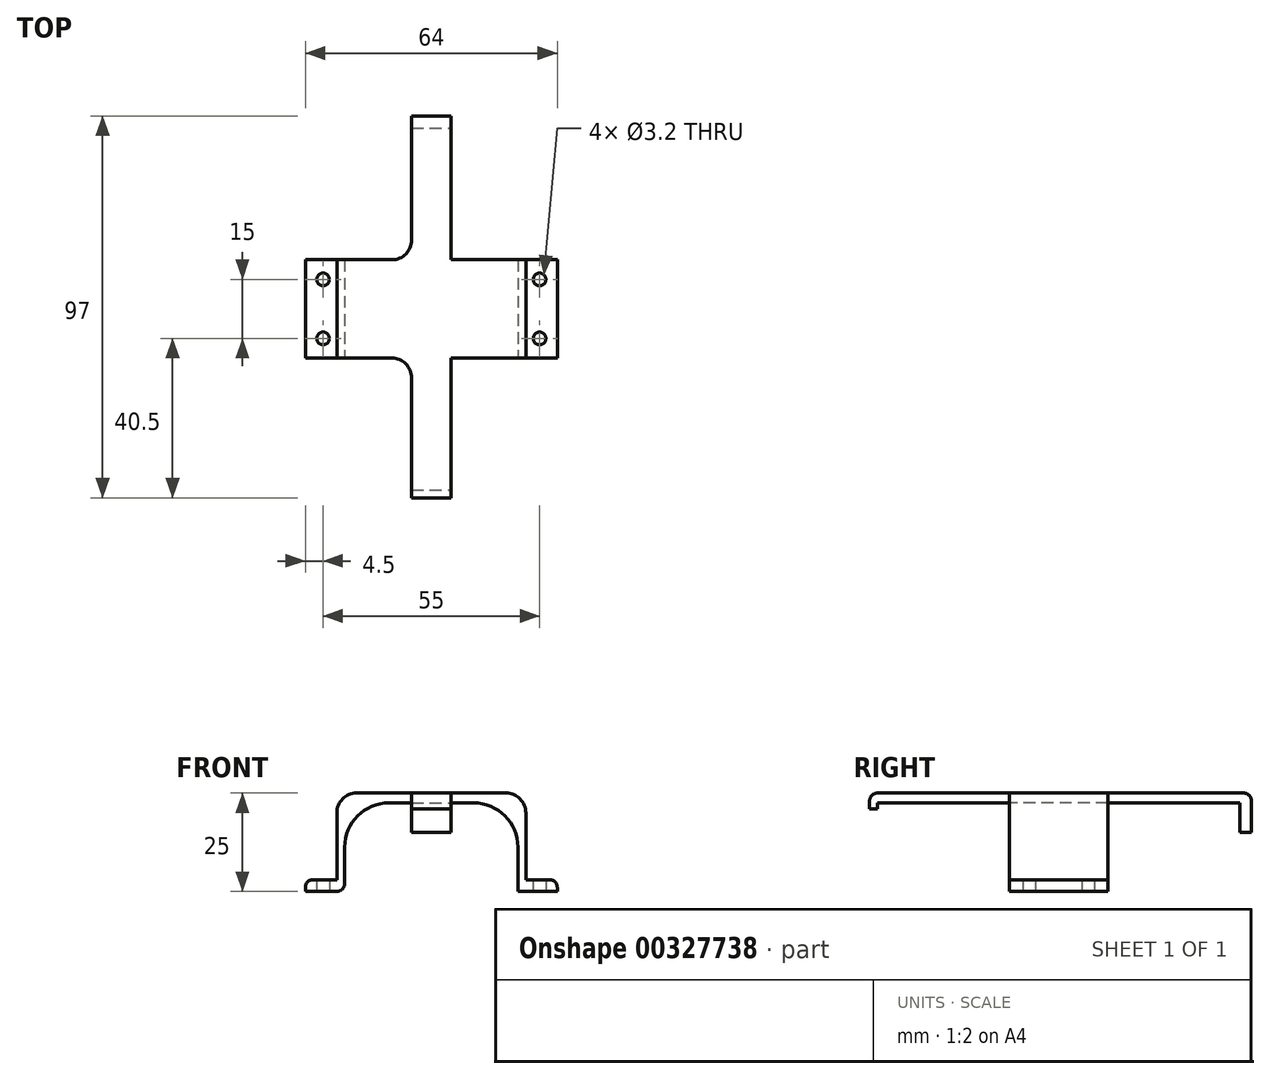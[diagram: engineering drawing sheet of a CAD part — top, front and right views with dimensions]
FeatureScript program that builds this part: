
annotation { "Feature Type Name" : "Feature", "Feature Type Description" : "" }
export const myFeature = defineFeature(function(context is Context, id is Id, definition is map)
    precondition{}
    {
        {
            var Q0;
            Q0=qCreatedBy(makeId("Front.planeOp"),FACE);
            var sketch = newSketch(context, id + "F0", { "sketchPlane" : qUnion([Q0])});
            skLineSegment(sketch, "E0.bottom", {"start": v(-24, 12.5) * mm, "end": v(24, 12.5) * mm});
            skLineSegment(sketch, "E0.top", {"start": v(-24, -12.5) * mm, "end": v(24, -12.5) * mm});
            skLineSegment(sketch, "E0.left", {"start": v(-24, 12.5) * mm, "end": v(-24, -12.5) * mm});
            skLineSegment(sketch, "E0.right", {"start": v(24, 12.5) * mm, "end": v(24, -12.5) * mm});
            skPoint(sketch, "E1", {"position": v(0, 12.5) * mm});
            skPoint(sketch, "E2", {"position": v(-24, 0) * mm});
            skSolve(sketch);
        }
        {
            var Q0;
            Q0=makeQuery(id+"F0.imprint","IMPRINT",FACE,{"disambiguationData":[TD([[makeQuery(id+"F0.imprint","IMPRINT",EDGE,{"derivedFrom":sQuery(id+"F0.wireOp",EDGE,"E0.bottom")}),-1.0]])]});
            extrude(context, id + "F1", {"entities" : qUnion([Q0]), "oppositeDirection" : true, "depth" : 25 * mm});
        }
        {
            var Q0;
            Q0=makeQuery(id+"F1.opExtrude","CAP_FACE",FACE,{"disambiguationData":[OSD([sQuery(id+"F0.wireOp",EDGE,"E0.bottom"),sQuery(id+"F0.wireOp",EDGE,"E0.top"),sQuery(id+"F0.wireOp",EDGE,"E0.left"),sQuery(id+"F0.wireOp",EDGE,"E0.right")])],"isStart":true});
            var sketch = newSketch(context, id + "F2", { "sketchPlane" : qUnion([Q0])});
            skArc(sketch, "E3", {"start": v(-10.75, -12.5) * mm, "mid": v(-22, -1.25) * mm, "end": v(-10.75, 10) * mm});
            skArc(sketch, "E4", {"start": v(10.75, -12.5) * mm, "mid": v(22, -1.25) * mm, "end": v(10.75, 10) * mm});
            skPoint(sketch, "E5", {"position": v(-22, -1.25) * mm});
            skPoint(sketch, "E6", {"position": v(22, -1.25) * mm});
            skLineSegment(sketch, "E7", {"start": v(-10.75, 10) * mm, "end": v(10.75, 10) * mm});
            skLineSegment(sketch, "E8", {"start": v(10.75, -12.5) * mm, "end": v(-10.75, -12.5) * mm});
            skPoint(sketch, "E9", {"position": v(0, 10) * mm});
            skLineSegment(sketch, "E10", {"start": v(-22, -1.25) * mm, "end": v(-22, -12.5) * mm});
            skLineSegment(sketch, "E11", {"start": v(-22, -12.5) * mm, "end": v(22, -12.5) * mm});
            skLineSegment(sketch, "E12", {"start": v(22, -12.5) * mm, "end": v(22, -1.25) * mm});
            skSolve(sketch);
        }
        {
            var Q0;
            {var subQ0=sQuery(id+"F2.wireOp",EDGE,"E7");Q0=makeQuery(id+"F2.imprint","IMPRINT",FACE,{"disambiguationData":[TD([[makeQuery(id+"F2.imprint","IMPRINT",EDGE,{"derivedFrom":subQ0}),-1.0]])]});}
            var Q1;
            {var subQ3=sQuery(id+"F2.wireOp",EDGE,"E10");Q1=makeQuery(id+"F2.imprint","IMPRINT",FACE,{"disambiguationData":[TD([[makeQuery(id+"F2.imprint","IMPRINT",EDGE,{"derivedFrom":subQ3}),1.0]])]});}
            var Q2;
            {var subQ3=sQuery(id+"F2.wireOp",EDGE,"E12");Q2=makeQuery(id+"F2.imprint","IMPRINT",FACE,{"disambiguationData":[TD([[makeQuery(id+"F2.imprint","IMPRINT",EDGE,{"derivedFrom":subQ3}),1.0]])]});}
            var Q3;
            Q3=makeQuery(id+"F1.opExtrude","CAP_FACE",FACE,{"disambiguationData":[OSD([sQuery(id+"F0.wireOp",EDGE,"E0.bottom"),sQuery(id+"F0.wireOp",EDGE,"E0.top"),sQuery(id+"F0.wireOp",EDGE,"E0.left"),sQuery(id+"F0.wireOp",EDGE,"E0.right")])],"isStart":false});
            extrude(context, id + "F3", {"entities" : qUnion([Q0, Q1, Q2]), "operationType" : NewBodyOperationType.REMOVE, "endBound" : BoundingType.UP_TO_SURFACE, "oppositeDirection" : true, "endBoundEntityFace" : qUnion([Q3]), "depth" : 25 * mm});
        }
        {
            var Q0;
            Q0=makeQuery(id+"F1.opExtrude","SWEPT_FACE",FACE,{"disambiguationData":[OSD([sQuery(id+"F0.wireOp",EDGE,"E0.bottom")])]});
            var sketch = newSketch(context, id + "F4", { "sketchPlane" : qUnion([Q0])});
            skLineSegment(sketch, "E13.bottom", {"start": v(-5, 58.5) * mm, "end": v(5, 58.5) * mm});
            skLineSegment(sketch, "E13.top", {"start": v(-5, -33.5) * mm, "end": v(5, -33.5) * mm});
            skLineSegment(sketch, "E13.left", {"start": v(-5, 58.5) * mm, "end": v(-5, -33.5) * mm});
            skLineSegment(sketch, "E13.right", {"start": v(5, 58.5) * mm, "end": v(5, -33.5) * mm});
            skPoint(sketch, "E14", {"position": v(0, 58.5) * mm});
            skPoint(sketch, "E15", {"position": v(5, 12.5) * mm});
            skPoint(sketch, "E16", {"position": v(24, 12.5) * mm});
            skSolve(sketch);
        }
        {
            var Q0;
            {var subQ0=sQuery(id+"F4.wireOp",EDGE,"E13.bottom");Q0=makeQuery(id+"F4.imprint","IMPRINT",FACE,{"disambiguationData":[TD([[makeQuery(id+"F4.imprint","IMPRINT",EDGE,{"derivedFrom":subQ0}),-1.0]])]});}
            var Q1;
            {var subQ0=sQuery(id+"F4.wireOp",EDGE,"E13.top");Q1=makeQuery(id+"F4.imprint","IMPRINT",FACE,{"disambiguationData":[TD([[makeQuery(id+"F4.imprint","IMPRINT",EDGE,{"derivedFrom":subQ0}),1.0]])]});}
            var Q2;
            Q2=makeQuery(id+"F3.boolean.opBoolean","COPY",FACE,{"derivedFrom":makeQuery(id+"F3.opExtrude","SWEPT_FACE",FACE,{"disambiguationData":[OSD([sQuery(id+"F2.wireOp",EDGE,"E7")])]})});
            extrude(context, id + "F5", {"entities" : qUnion([Q0, Q1]), "operationType" : NewBodyOperationType.ADD, "endBound" : BoundingType.UP_TO_SURFACE, "oppositeDirection" : true, "endBoundEntityFace" : qUnion([Q2]), "depth" : 25 * mm});
        }
        {
            var Q0;
            Q0=makeQuery(id+"F5.opExtrude","SWEPT_FACE",FACE,{"disambiguationData":[OSD([sQuery(id+"F4.wireOp",EDGE,"E13.top")])]});
            var sketch = newSketch(context, id + "F6", { "sketchPlane" : qUnion([Q0])});
            skLineSegment(sketch, "E17.bottom", {"start": v(-5, 12.5) * mm, "end": v(5, 12.5) * mm});
            skLineSegment(sketch, "E17.top", {"start": v(-5, 8.5) * mm, "end": v(5, 8.5) * mm});
            skLineSegment(sketch, "E17.left", {"start": v(-5, 12.5) * mm, "end": v(-5, 8.5) * mm});
            skLineSegment(sketch, "E17.right", {"start": v(5, 12.5) * mm, "end": v(5, 8.5) * mm});
            skSolve(sketch);
        }
        {
            var Q0;
            {var subQ0=sQuery(id+"F6.wireOp",EDGE,"E17.top");Q0=makeQuery(id+"F6.imprint","IMPRINT",FACE,{"disambiguationData":[TD([[makeQuery(id+"F6.imprint","IMPRINT",EDGE,{"derivedFrom":subQ0}),1.0]])]});}
            var Q1;
            {var subQ0=sQuery(id+"F6.wireOp",EDGE,"E17.bottom");Q1=makeQuery(id+"F6.imprint","IMPRINT",FACE,{"disambiguationData":[TD([[makeQuery(id+"F6.imprint","IMPRINT",EDGE,{"derivedFrom":subQ0}),-1.0]])]});}
            extrude(context, id + "F7", {"entities" : qUnion([Q0, Q1]), "operationType" : NewBodyOperationType.ADD, "depth" : 2 * mm});
        }
        {
            var Q0;
            Q0=makeQuery(id+"F5.opExtrude","SWEPT_FACE",FACE,{"disambiguationData":[OSD([sQuery(id+"F4.wireOp",EDGE,"E13.bottom")])]});
            var sketch = newSketch(context, id + "F8", { "sketchPlane" : qUnion([Q0])});
            skLineSegment(sketch, "E18.bottom", {"start": v(-5, 12.5) * mm, "end": v(5, 12.5) * mm});
            skLineSegment(sketch, "E18.top", {"start": v(-5, 2.5) * mm, "end": v(5, 2.5) * mm});
            skLineSegment(sketch, "E18.left", {"start": v(-5, 12.5) * mm, "end": v(-5, 2.5) * mm});
            skLineSegment(sketch, "E18.right", {"start": v(5, 12.5) * mm, "end": v(5, 2.5) * mm});
            skSolve(sketch);
        }
        {
            var Q0;
            {var subQ0=sQuery(id+"F8.wireOp",EDGE,"E18.top");Q0=makeQuery(id+"F8.imprint","IMPRINT",FACE,{"disambiguationData":[TD([[makeQuery(id+"F8.imprint","IMPRINT",EDGE,{"derivedFrom":subQ0}),1.0]])]});}
            var Q1;
            {var subQ0=sQuery(id+"F8.wireOp",EDGE,"E18.bottom");Q1=makeQuery(id+"F8.imprint","IMPRINT",FACE,{"disambiguationData":[TD([[makeQuery(id+"F8.imprint","IMPRINT",EDGE,{"derivedFrom":subQ0}),1.0]])]});}
            extrude(context, id + "F9", {"entities" : qUnion([Q0, Q1]), "operationType" : NewBodyOperationType.ADD, "depth" : 3 * mm});
        }
        {
            var Q0;
            {var subQ0=sQuery(id+"F0.wireOp",EDGE,"E0.right");var subQ2=sQuery(id+"F0.wireOp",EDGE,"E0.top");Q0=makeQuery(id+"F3.boolean.opBoolean","SPLIT",FACE,{"disambiguationData":[TD([makeQuery(id+"F1.opExtrude","SWEPT_FACE",FACE,{"disambiguationData":[OSD([subQ0])]})])],"derivedFrom":makeQuery(id+"F1.opExtrude","SWEPT_FACE",FACE,{"disambiguationData":[OSD([subQ2])]})});}
            var sketch = newSketch(context, id + "F10", { "sketchPlane" : qUnion([Q0])});
            skLineSegment(sketch, "E19.bottom", {"start": v(24, 0) * mm, "end": v(32, 0) * mm});
            skLineSegment(sketch, "E19.top", {"start": v(24, -25) * mm, "end": v(32, -25) * mm});
            skLineSegment(sketch, "E19.left", {"start": v(24, 0) * mm, "end": v(24, -25) * mm});
            skLineSegment(sketch, "E19.right", {"start": v(32, 0) * mm, "end": v(32, -25) * mm});
            skLineSegment(sketch, "E20.0.0", {"start": v(-24, -25) * mm, "end": v(-22, -25) * mm, "construction": true});
            skLineSegment(sketch, "E20.0.1", {"start": v(-22, -25) * mm, "end": v(-22, 0) * mm, "construction": true});
            skLineSegment(sketch, "E20.0.2", {"start": v(-22, 0) * mm, "end": v(-24, 0) * mm, "construction": true});
            skLineSegment(sketch, "E20.0.3", {"start": v(-24, 0) * mm, "end": v(-24, -25) * mm, "construction": true});
            skLineSegment(sketch, "E21.bottom", {"start": v(-24, 0) * mm, "end": v(-32, 0) * mm});
            skLineSegment(sketch, "E21.top", {"start": v(-24, -25) * mm, "end": v(-32, -25) * mm});
            skLineSegment(sketch, "E21.left", {"start": v(-24, 0) * mm, "end": v(-24, -25) * mm});
            skLineSegment(sketch, "E21.right", {"start": v(-32, 0) * mm, "end": v(-32, -25) * mm});
            skSolve(sketch);
        }
        {
            var Q0;
            Q0=makeQuery(id+"F10.imprint","IMPRINT",FACE,{"disambiguationData":[TD([[makeQuery(id+"F10.imprint","IMPRINT",EDGE,{"derivedFrom":sQuery(id+"F10.wireOp",EDGE,"E21.bottom")}),1.0]])]});
            var Q1;
            Q1=makeQuery(id+"F10.imprint","IMPRINT",FACE,{"disambiguationData":[TD([[makeQuery(id+"F10.imprint","IMPRINT",EDGE,{"derivedFrom":sQuery(id+"F10.wireOp",EDGE,"E19.bottom")}),-1.0]])]});
            extrude(context, id + "F11", {"entities" : qUnion([Q0, Q1]), "operationType" : NewBodyOperationType.ADD, "oppositeDirection" : true, "depth" : 3 * mm});
        }
        {
            var Q0;
            {var subQ0=sQuery(id+"F0.wireOp",EDGE,"E0.right");var subQ2=sQuery(id+"F0.wireOp",EDGE,"E0.top");Q0=makeQuery(id+"F11.boolean.opBoolean","MERGE",FACE,{"derivedFrom":[makeQuery(id+"F3.boolean.opBoolean","SPLIT",FACE,{"disambiguationData":[TD([makeQuery(id+"F1.opExtrude","SWEPT_FACE",FACE,{"disambiguationData":[OSD([subQ0])]})])],"derivedFrom":makeQuery(id+"F1.opExtrude","SWEPT_FACE",FACE,{"disambiguationData":[OSD([subQ2])]})}),makeQuery(id+"F11.opExtrude","CAP_FACE",FACE,{"disambiguationData":[OSD([sQuery(id+"F10.wireOp",EDGE,"E19.bottom"),sQuery(id+"F10.wireOp",EDGE,"E19.top"),sQuery(id+"F10.wireOp",EDGE,"E19.left"),sQuery(id+"F10.wireOp",EDGE,"E19.right")])],"isStart":true})]});}
            var sketch = newSketch(context, id + "F12", { "sketchPlane" : qUnion([Q0])});
            skCircle(sketch, "E22", {"center": v(27.5, -5) * mm, "radius": 1.6 * mm});
            skCircle(sketch, "E23", {"center": v(27.5, -20) * mm, "radius": 1.6 * mm});
            skCircle(sketch, "E24", {"center": v(-27.5, -5) * mm, "radius": 1.6 * mm});
            skCircle(sketch, "E25", {"center": v(-27.5, -20) * mm, "radius": 1.6 * mm});
            skLineSegment(sketch, "E26", {"start": v(-27.5, -5) * mm, "end": v(-27.5, -20) * mm, "construction": true});
            skLineSegment(sketch, "E27", {"start": v(27.5, -5) * mm, "end": v(27.5, -20) * mm, "construction": true});
            skLineSegment(sketch, "E28", {"start": v(-27.5, -5) * mm, "end": v(27.5, -5) * mm, "construction": true});
            skPoint(sketch, "E29", {"position": v(0, -5) * mm});
            skPoint(sketch, "E30", {"position": v(-27.5, -12.5) * mm});
            skPoint(sketch, "E31", {"position": v(32, -12.5) * mm});
            skSolve(sketch);
        }
        {
            var Q0;
            Q0=makeQuery(id+"F12.imprint","IMPRINT",FACE,{"disambiguationData":[TD([[makeQuery(id+"F12.imprint","IMPRINT",EDGE,{"derivedFrom":sQuery(id+"F12.wireOp",EDGE,"E24")}),1.0]])]});
            var Q1;
            Q1=makeQuery(id+"F12.imprint","IMPRINT",FACE,{"disambiguationData":[TD([[makeQuery(id+"F12.imprint","IMPRINT",EDGE,{"derivedFrom":sQuery(id+"F12.wireOp",EDGE,"E25")}),1.0]])]});
            var Q2;
            Q2=makeQuery(id+"F12.imprint","IMPRINT",FACE,{"disambiguationData":[TD([[makeQuery(id+"F12.imprint","IMPRINT",EDGE,{"derivedFrom":sQuery(id+"F12.wireOp",EDGE,"E23")}),1.0]])]});
            var Q3;
            Q3=makeQuery(id+"F12.imprint","IMPRINT",FACE,{"disambiguationData":[TD([[makeQuery(id+"F12.imprint","IMPRINT",EDGE,{"derivedFrom":sQuery(id+"F12.wireOp",EDGE,"E22")}),1.0]])]});
            extrude(context, id + "F13", {"entities" : qUnion([Q0, Q1, Q2, Q3]), "operationType" : NewBodyOperationType.REMOVE, "endBound" : BoundingType.UP_TO_NEXT, "oppositeDirection" : true, "depth" : 25 * mm});
        }
        {
            var Q0;
            Q0=makeQuery(id+"F1.opExtrude","SWEPT_EDGE",EDGE,{"disambiguationData":[OSD([sQuery(id+"F0.wireOp",EDGE,"E0.bottom"),sQuery(id+"F0.wireOp",EDGE,"E0.left")])]});
            var Q1;
            Q1=makeQuery(id+"F1.opExtrude","SWEPT_EDGE",EDGE,{"disambiguationData":[OSD([sQuery(id+"F0.wireOp",EDGE,"E0.bottom"),sQuery(id+"F0.wireOp",EDGE,"E0.right")])]});
            var Q2;
            {var subQ0=sQuery(id+"F4.wireOp",EDGE,"E13.left");var subQ1=sQuery(id+"F0.wireOp",EDGE,"E0.bottom");Q2=makeQuery(id+"F5.opExtrude","SWEPT_EDGE",EDGE,{"disambiguationData":[OSD([subQ1,subQ0]),TDD([makeQuery(id+"F4.imprint","INTERSECT",VERTEX,{"derivedFrom":[makeQuery(id+"F1.opExtrude","CAP_EDGE",EDGE,{"disambiguationData":[OSD([subQ1])],"isStart":false}),subQ0]})])]});}
            var Q3;
            {var subQ0=sQuery(id+"F4.wireOp",EDGE,"E13.left");var subQ1=sQuery(id+"F0.wireOp",EDGE,"E0.bottom");Q3=makeQuery(id+"F5.opExtrude","SWEPT_EDGE",EDGE,{"disambiguationData":[OSD([subQ1,subQ0]),TDD([makeQuery(id+"F4.imprint","INTERSECT",VERTEX,{"derivedFrom":[makeQuery(id+"F1.opExtrude","CAP_EDGE",EDGE,{"disambiguationData":[OSD([subQ1])],"isStart":true}),subQ0]})])]});}
            var Q4;
            {var subQ0=sQuery(id+"F4.wireOp",EDGE,"E13.right");var subQ1=sQuery(id+"F0.wireOp",EDGE,"E0.bottom");Q4=makeQuery(id+"F5.opExtrude","SWEPT_EDGE",EDGE,{"disambiguationData":[OSD([subQ1,subQ0]),TDD([makeQuery(id+"F4.imprint","INTERSECT",VERTEX,{"derivedFrom":[makeQuery(id+"F1.opExtrude","CAP_EDGE",EDGE,{"disambiguationData":[OSD([subQ1])],"isStart":true}),subQ0]})])]});}
            var Q5;
            {var subQ0=sQuery(id+"F4.wireOp",EDGE,"E13.right");var subQ1=sQuery(id+"F0.wireOp",EDGE,"E0.bottom");Q5=makeQuery(id+"F5.opExtrude","SWEPT_EDGE",EDGE,{"disambiguationData":[OSD([subQ1,subQ0]),TDD([makeQuery(id+"F4.imprint","INTERSECT",VERTEX,{"derivedFrom":[makeQuery(id+"F1.opExtrude","CAP_EDGE",EDGE,{"disambiguationData":[OSD([subQ1])],"isStart":false}),subQ0]})])]});}
            fillet(context, id + "F14", {"entities" : qUnion([Q0, Q1, Q2, Q3, Q4, Q5]), "radius" : 5 * mm, "tangentPropagation" : true, "allowEdgeOverflow" : false});
        }
        {
            var Q0;
            Q0=makeQuery(id+"F9.opExtrude","CAP_EDGE",EDGE,{"disambiguationData":[OSD([sQuery(id+"F8.wireOp",EDGE,"E18.bottom")])],"isStart":false});
            var Q1;
            Q1=makeQuery(id+"F7.opExtrude","CAP_EDGE",EDGE,{"disambiguationData":[OSD([sQuery(id+"F6.wireOp",EDGE,"E17.bottom")])],"isStart":false});
            var Q2;
            Q2=makeQuery(id+"F3.boolean.opBoolean","COPY",EDGE,{"derivedFrom":makeQuery(id+"F3.opExtrude","SWEPT_EDGE",EDGE,{"disambiguationData":[OSD([sQuery(id+"F0.wireOp",EDGE,"E0.top"),sQuery(id+"F2.wireOp",EDGE,"E11"),sQuery(id+"F2.wireOp",EDGE,"E12")])]})});
            var Q3;
            Q3=makeQuery(id+"F3.boolean.opBoolean","COPY",EDGE,{"derivedFrom":makeQuery(id+"F3.opExtrude","SWEPT_EDGE",EDGE,{"disambiguationData":[OSD([sQuery(id+"F0.wireOp",EDGE,"E0.top"),sQuery(id+"F2.wireOp",EDGE,"E10"),sQuery(id+"F2.wireOp",EDGE,"E11")])]})});
            var Q4;
            Q4=makeQuery(id+"F11.opExtrude","CAP_EDGE",EDGE,{"disambiguationData":[OSD([sQuery(id+"F10.wireOp",EDGE,"E21.right")])],"isStart":false});
            var Q5;
            Q5=makeQuery(id+"F11.opExtrude","CAP_EDGE",EDGE,{"disambiguationData":[OSD([sQuery(id+"F10.wireOp",EDGE,"E19.right")])],"isStart":false});
            fillet(context, id + "F15", {"entities" : qUnion([Q0, Q1, Q2, Q3, Q4, Q5]), "radius" : 2 * mm, "tangentPropagation" : true, "allowEdgeOverflow" : false});
        }
    });
